# Revit family: 1630
name_source: partatom
category: Plumbing Fixtures
revit_build: Autodesk Revit MEP 2016 (Build: 20150220_1215(x64)
units: mm (PartAtom-declared; Revit-internal decimal feet)

## family parameters
Cut with Voids When Loaded = No
Host = Face
OmniClass Number = 23.45.05.14.14.27
OmniClass Title = Service Sinks
Part Type = Normal
Room Calculation Point = No
Round Connector Dimension = Use Diameter
Shared = Yes

## types (1)
- 1630
    1630 Mop Sink, 24" x 24" x 10” Deep = Yes
    Assembly Code = D2010440
    BDS - Beehive Dome Strainer = No
    CW Connection = No
    CWFU = 3
    Connection Size = 3"
    Default Elevation = 0"
    Description = Penal-Ware 1630 Series Stainless Steel Mop Sink
    Drain Extension = 1/2"
    Edge Thickness = 2"
    HW Connection = No
    HWFU = 3
    Height = 10"
    KDG3 - Rubber Drain Gasket for 3" Waste Pipe = No
    KFC Chrome Utility Faucet, Hot & Cold, 8” Centerset (not Vandal Resistant; Shipped Loose) = No
    KH36 - Hose 36" Long with Wall Hanger = No
    KMH 3 Mop Hanger Stainless Steel Bracket = No
    KWG24 Stainless Steel Wall Guard, 12” x 24” Specify Quantity: = No
    Length = 24"
    Manufacturer = Acorn
    Material = Metal-Acorn-Stainless Steel_Brushed
    Model = 1630
    Product Documentation Link = https://www.acorneng.com
    Product Page URL = https://www.acorneng.com
    TA - Threshold Anchors = No
    TF1 Tiling Flange, Rear Side = No
    TF2 Tiling Flange, Two Adjacent Sides  (Rear & Left Side) = No
    TF2 Tiling Flange, Two Adjacent Sides  (Rear & Right Side) = No
    TF3 Tiling Flange, Three Sides (Rear, Right and Left Sides) = No
    Top edge to Sink Floor = 8 1/4"
    URL = http://www.acorneng.com
    Vent Connection = No
    WFU = 4
    Warranty Documentation Link = www.acorneng.com/terms-and-conditions
    Waste Connection = Yes
    Width = 24"

## geometry (parser evidence)
native form markers: Sweep x3
no freeform markers — native parametric forms only
